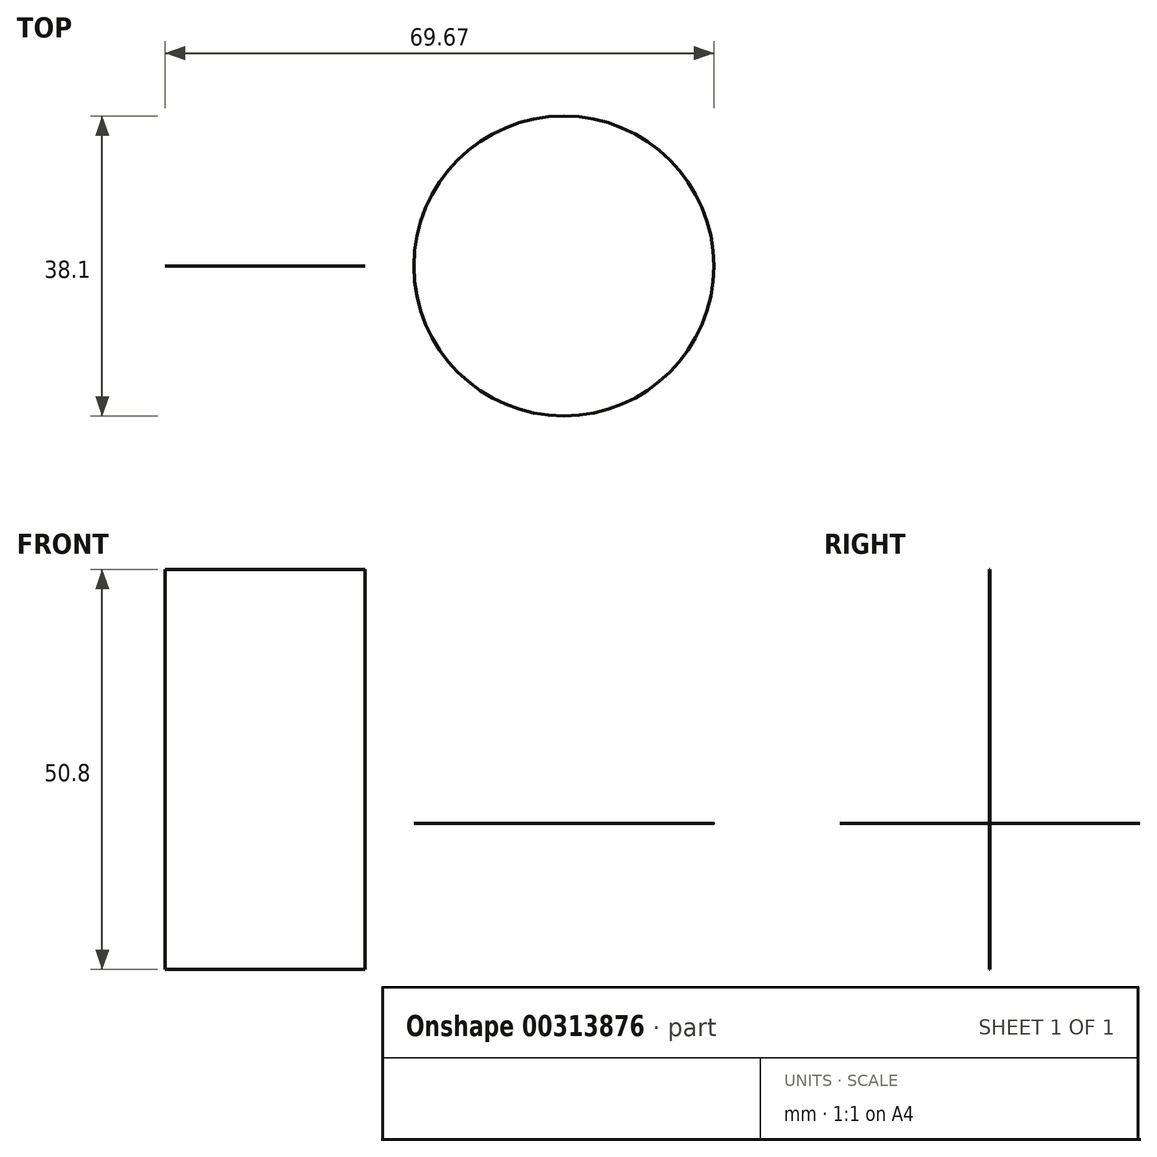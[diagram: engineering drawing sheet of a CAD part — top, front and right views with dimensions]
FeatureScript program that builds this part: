
annotation { "Feature Type Name" : "Feature", "Feature Type Description" : "" }
export const myFeature = defineFeature(function(context is Context, id is Id, definition is map)
    precondition{}
    {
        {
            var Q0;
            Q0=qCreatedBy(makeId("Top.planeOp"),FACE);
            var sketch = newSketch(context, id + "F0", { "sketchPlane" : qUnion([Q0])});
            skCircle(sketch, "E0", {"center": v(0, 0) * mm, "radius": 19.05 * mm});
            skSolve(sketch);
        }
        {
            var Q0;
            Q0=qCreatedBy(makeId("Front.planeOp"),FACE);
            var sketch = newSketch(context, id + "F1", { "sketchPlane" : qUnion([Q0])});
            skLineSegment(sketch, "E1.bottom", {"start": v(-50.62, 32.27) * mm, "end": v(-25.22, 32.27) * mm});
            skLineSegment(sketch, "E1.top", {"start": v(-50.62, -18.53) * mm, "end": v(-25.22, -18.53) * mm});
            skLineSegment(sketch, "E1.left", {"start": v(-50.62, 32.27) * mm, "end": v(-50.62, -18.53) * mm});
            skLineSegment(sketch, "E1.right", {"start": v(-25.22, 32.27) * mm, "end": v(-25.22, -18.53) * mm});
            skSolve(sketch);
        }
        {
            var Q0;
            Q0=makeQuery(id+"F1.imprint","IMPRINT",FACE,{"disambiguationData":[TD([[makeQuery(id+"F1.imprint","IMPRINT",EDGE,{"derivedFrom":sQuery(id+"F1.wireOp",EDGE,"E1.bottom")}),-1.0]])]});
            extrude(context, id + "F2", {"entities" : qUnion([Q0]), "depth" : 0.03 * mm});
        }
        {
            var Q0;
            Q0=makeQuery(id+"F0.imprint","IMPRINT",FACE,{"disambiguationData":[TD([[makeQuery(id+"F0.imprint","IMPRINT",EDGE,{"derivedFrom":sQuery(id+"F0.wireOp",EDGE,"E0")}),1.0]])]});
            extrude(context, id + "F3", {"entities" : qUnion([Q0]), "depth" : 0.03 * mm});
        }
    });
